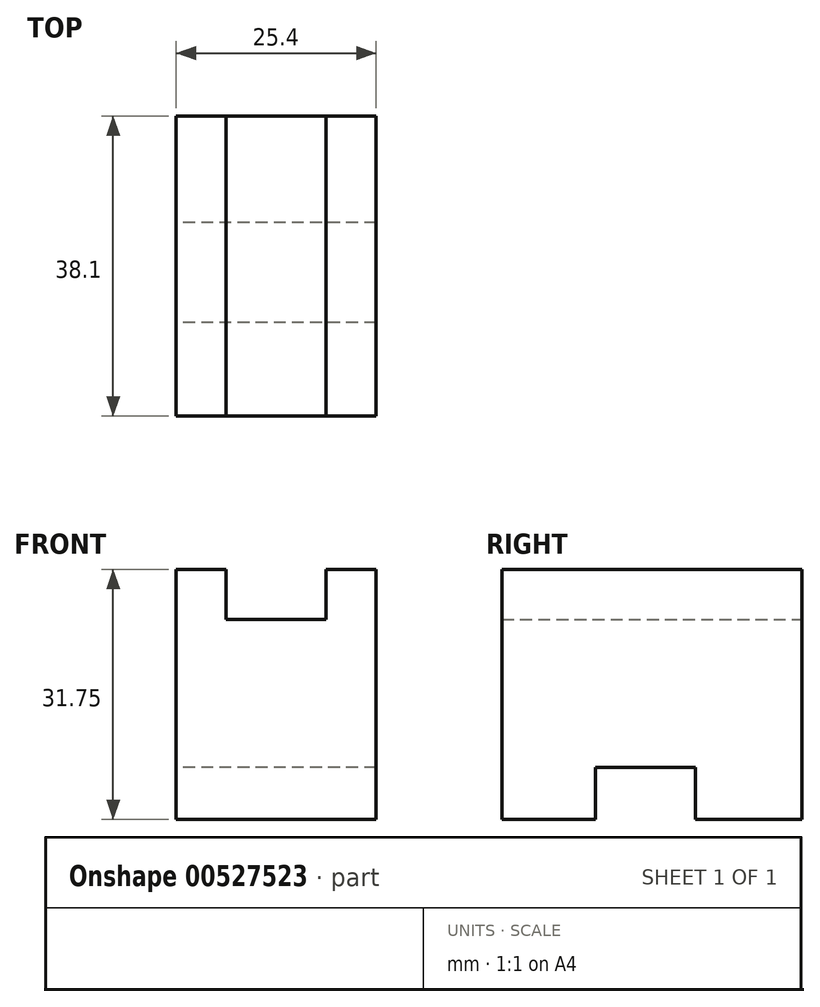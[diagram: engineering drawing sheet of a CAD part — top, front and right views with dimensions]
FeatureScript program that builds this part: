
annotation { "Feature Type Name" : "Feature", "Feature Type Description" : "" }
export const myFeature = defineFeature(function(context is Context, id is Id, definition is map)
    precondition{}
    {
        {
            var Q0;
            Q0=qCreatedBy(makeId("Front.planeOp"),FACE);
            var sketch = newSketch(context, id + "F0", { "sketchPlane" : qUnion([Q0])});
            skLineSegment(sketch, "E0", {"start": v(0, 0) * mm, "end": v(0, 31.75) * mm});
            skLineSegment(sketch, "E1", {"start": v(0, 31.75) * mm, "end": v(6.35, 31.75) * mm});
            skLineSegment(sketch, "E2", {"start": v(6.35, 31.75) * mm, "end": v(6.35, 25.4) * mm});
            skLineSegment(sketch, "E3", {"start": v(6.35, 25.4) * mm, "end": v(19.05, 25.4) * mm});
            skLineSegment(sketch, "E4", {"start": v(19.05, 25.4) * mm, "end": v(19.05, 31.75) * mm});
            skLineSegment(sketch, "E5", {"start": v(19.05, 31.75) * mm, "end": v(25.4, 31.75) * mm});
            skLineSegment(sketch, "E6", {"start": v(25.4, 31.75) * mm, "end": v(25.4, 0) * mm});
            skLineSegment(sketch, "E7", {"start": v(25.4, 0) * mm, "end": v(0, 0) * mm});
            skSolve(sketch);
        }
        {
            var Q0;
            Q0=makeQuery(id+"F0.imprint","IMPRINT",FACE,{"disambiguationData":[TD([[makeQuery(id+"F0.imprint","IMPRINT",EDGE,{"derivedFrom":sQuery(id+"F0.wireOp",EDGE,"E0")}),-1.0]])]});
            extrude(context, id + "F1", {"entities" : qUnion([Q0]), "depth" : 38.1 * mm, "offsetDistance" : 25.4 * mm});
        }
        {
            var Q0;
            Q0=makeQuery(id+"F1.opExtrude","SWEPT_FACE",FACE,{"disambiguationData":[OSD([sQuery(id+"F0.wireOp",EDGE,"E0")])]});
            var sketch = newSketch(context, id + "F2", { "sketchPlane" : qUnion([Q0])});
            skLineSegment(sketch, "E8", {"start": v(13.53, 0) * mm, "end": v(13.53, 6.62) * mm});
            skLineSegment(sketch, "E9", {"start": v(13.53, 6.62) * mm, "end": v(26.23, 6.62) * mm});
            skLineSegment(sketch, "E10", {"start": v(26.23, 6.62) * mm, "end": v(26.23, 0) * mm});
            skLineSegment(sketch, "E11", {"start": v(26.23, 0) * mm, "end": v(13.53, 0) * mm});
            skSolve(sketch);
        }
        {
            var Q0;
            Q0=makeQuery(id+"F2.imprint","IMPRINT",FACE,{"disambiguationData":[TD([[makeQuery(id+"F2.imprint","IMPRINT",EDGE,{"derivedFrom":sQuery(id+"F2.wireOp",EDGE,"E8")}),-1.0]])]});
            extrude(context, id + "F3", {"entities" : qUnion([Q0]), "operationType" : NewBodyOperationType.REMOVE, "oppositeDirection" : true, "depth" : 25.4 * mm, "offsetDistance" : 25.4 * mm});
        }
    });
